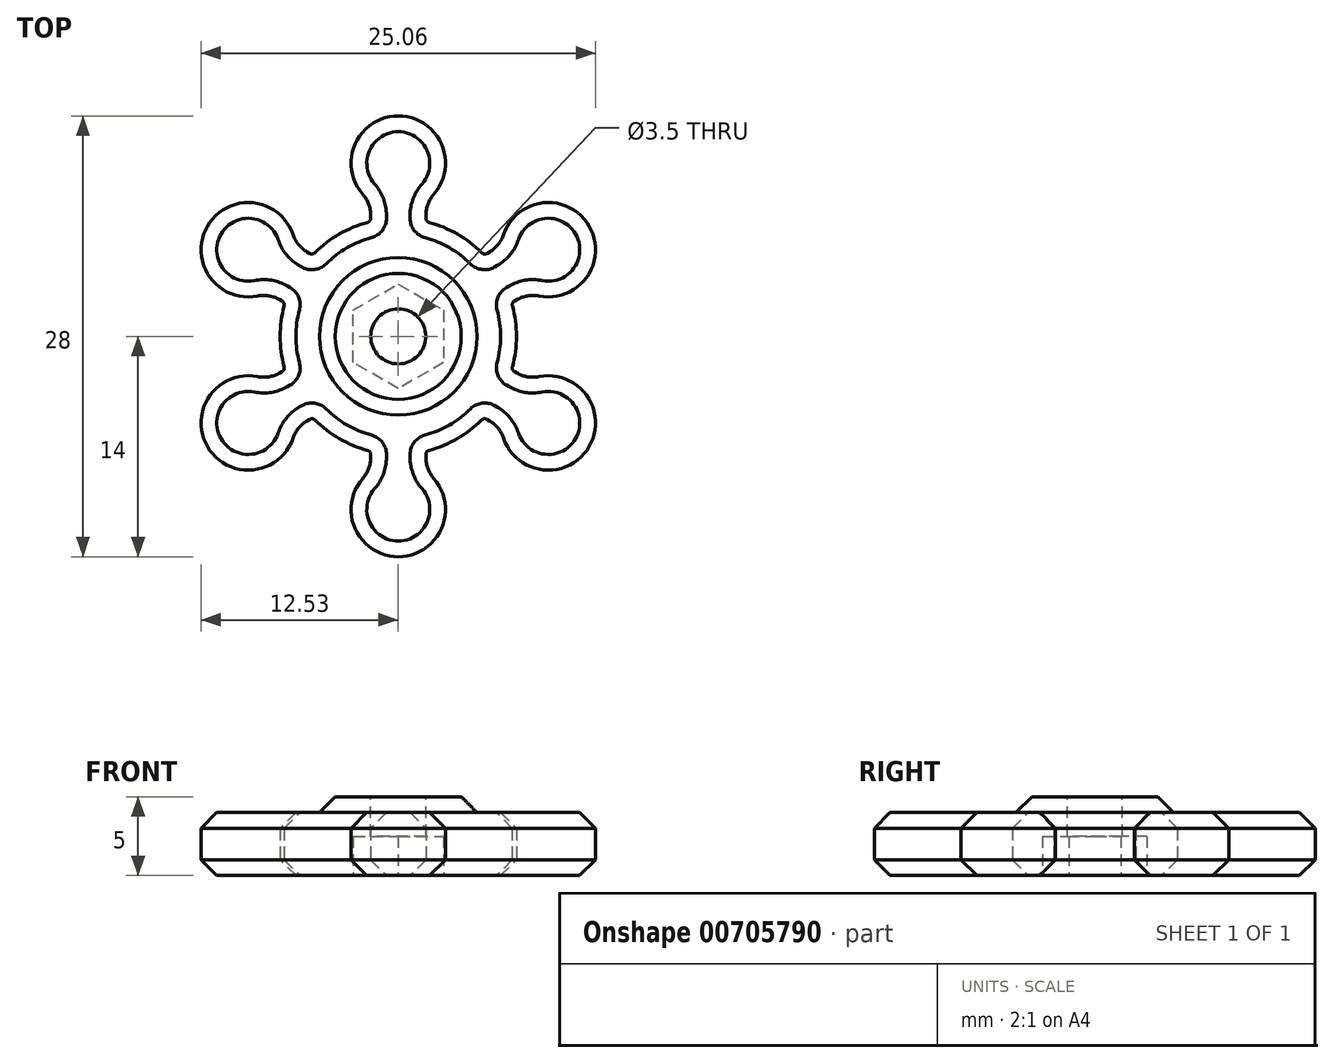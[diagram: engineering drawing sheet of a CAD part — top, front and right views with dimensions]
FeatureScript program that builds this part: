
annotation { "Feature Type Name" : "Feature", "Feature Type Description" : "" }
export const myFeature = defineFeature(function(context is Context, id is Id, definition is map)
    precondition{}
    {
        {
            var Q0;
            Q0=qCreatedBy(makeId("Top.planeOp"),FACE);
            var sketch = newSketch(context, id + "F0", { "sketchPlane" : qUnion([Q0])});
            skArc(sketch, "E0", {"start": v(-1.95, 7.24) * mm, "mid": v(-3.75, 6.5) * mm, "end": v(-5.3, 5.31) * mm});
            skArc(sketch, "E1", {"start": v(2.25, 9.02) * mm, "mid": v(0, 14) * mm, "end": v(-2.25, 9.02) * mm});
            skLineSegment(sketch, "E2.left", {"start": v(-1.75, 7.5) * mm, "end": v(-1.75, 7.7) * mm});
            skLineSegment(sketch, "E2.right", {"start": v(1.75, 7.5) * mm, "end": v(1.75, 7.7) * mm});
            skPoint(sketch, "E3.orphan", {"position": v(-1.75, 0) * mm});
            skPoint(sketch, "E4.visualSharp", {"position": v(-1.75, 8.56) * mm});
            skArc(sketch, "E4.filletArc", {"start": v(-1.75, 7.7) * mm, "mid": v(-1.88, 8.4) * mm, "end": v(-2.25, 9.02) * mm});
            skPoint(sketch, "E5.visualSharp", {"position": v(1.75, 8.56) * mm});
            skArc(sketch, "E5.filletArc", {"start": v(2.25, 9.02) * mm, "mid": v(1.88, 8.4) * mm, "end": v(1.75, 7.7) * mm});
            skPoint(sketch, "E6.visualSharp", {"position": v(1.75, 7.3) * mm});
            skArc(sketch, "E6.filletArc", {"start": v(1.75, 7.5) * mm, "mid": v(1.8, 7.34) * mm, "end": v(1.95, 7.24) * mm});
            skPoint(sketch, "E7.visualSharp", {"position": v(-1.75, 7.3) * mm});
            skArc(sketch, "E7.filletArc", {"start": v(-1.95, 7.24) * mm, "mid": v(-1.8, 7.34) * mm, "end": v(-1.75, 7.5) * mm});
            skArc(sketch, "E8.1.0", {"start": v(-6.68, 6.46) * mm, "mid": v(-12.12, 7) * mm, "end": v(-8.93, 2.56) * mm});
            skArc(sketch, "E8.1.1", {"start": v(-6.68, 6.46) * mm, "mid": v(-6.33, 5.83) * mm, "end": v(-5.79, 5.36) * mm});
            skArc(sketch, "E8.1.2", {"start": v(-7.54, 2.33) * mm, "mid": v(-8.21, 2.57) * mm, "end": v(-8.93, 2.56) * mm});
            skLineSegment(sketch, "E8.1.3", {"start": v(-7.37, 2.24) * mm, "end": v(-7.54, 2.33) * mm});
            skArc(sketch, "E8.1.4", {"start": v(-7.25, 1.93) * mm, "mid": v(-7.26, 2.1) * mm, "end": v(-7.37, 2.24) * mm});
            skLineSegment(sketch, "E8.1.5", {"start": v(-5.62, 5.27) * mm, "end": v(-5.79, 5.36) * mm});
            skArc(sketch, "E8.1.6", {"start": v(-5.62, 5.27) * mm, "mid": v(-5.45, 5.23) * mm, "end": v(-5.3, 5.31) * mm});
            skArc(sketch, "E8.2.0", {"start": v(-8.93, -2.56) * mm, "mid": v(-12.12, -7) * mm, "end": v(-6.68, -6.46) * mm});
            skArc(sketch, "E8.2.1", {"start": v(-8.93, -2.56) * mm, "mid": v(-8.21, -2.57) * mm, "end": v(-7.54, -2.33) * mm});
            skArc(sketch, "E8.2.2", {"start": v(-5.79, -5.36) * mm, "mid": v(-6.33, -5.83) * mm, "end": v(-6.68, -6.46) * mm});
            skLineSegment(sketch, "E8.2.3", {"start": v(-5.62, -5.27) * mm, "end": v(-5.79, -5.36) * mm});
            skArc(sketch, "E8.2.4", {"start": v(-5.3, -5.31) * mm, "mid": v(-5.45, -5.23) * mm, "end": v(-5.62, -5.27) * mm});
            skLineSegment(sketch, "E8.2.5", {"start": v(-7.37, -2.24) * mm, "end": v(-7.54, -2.33) * mm});
            skArc(sketch, "E8.2.6", {"start": v(-7.37, -2.24) * mm, "mid": v(-7.26, -2.1) * mm, "end": v(-7.25, -1.93) * mm});
            skArc(sketch, "E8.3.0", {"start": v(-2.25, -9.02) * mm, "mid": v(0, -14) * mm, "end": v(2.25, -9.02) * mm});
            skArc(sketch, "E8.3.1", {"start": v(-2.25, -9.02) * mm, "mid": v(-1.88, -8.4) * mm, "end": v(-1.75, -7.7) * mm});
            skArc(sketch, "E8.3.2", {"start": v(1.75, -7.7) * mm, "mid": v(1.88, -8.4) * mm, "end": v(2.25, -9.02) * mm});
            skLineSegment(sketch, "E8.3.3", {"start": v(1.75, -7.5) * mm, "end": v(1.75, -7.7) * mm});
            skArc(sketch, "E8.3.4", {"start": v(1.95, -7.24) * mm, "mid": v(1.8, -7.34) * mm, "end": v(1.75, -7.5) * mm});
            skLineSegment(sketch, "E8.3.5", {"start": v(-1.75, -7.5) * mm, "end": v(-1.75, -7.7) * mm});
            skArc(sketch, "E8.3.6", {"start": v(-1.75, -7.5) * mm, "mid": v(-1.8, -7.34) * mm, "end": v(-1.95, -7.24) * mm});
            skArc(sketch, "E8.4.0", {"start": v(6.68, -6.46) * mm, "mid": v(12.12, -7) * mm, "end": v(8.93, -2.56) * mm});
            skArc(sketch, "E8.4.1", {"start": v(6.68, -6.46) * mm, "mid": v(6.33, -5.83) * mm, "end": v(5.79, -5.36) * mm});
            skArc(sketch, "E8.4.2", {"start": v(7.54, -2.33) * mm, "mid": v(8.21, -2.57) * mm, "end": v(8.93, -2.56) * mm});
            skLineSegment(sketch, "E8.4.3", {"start": v(7.37, -2.24) * mm, "end": v(7.54, -2.33) * mm});
            skArc(sketch, "E8.4.4", {"start": v(7.25, -1.93) * mm, "mid": v(7.26, -2.1) * mm, "end": v(7.37, -2.24) * mm});
            skLineSegment(sketch, "E8.4.5", {"start": v(5.62, -5.27) * mm, "end": v(5.79, -5.36) * mm});
            skArc(sketch, "E8.4.6", {"start": v(5.62, -5.27) * mm, "mid": v(5.45, -5.23) * mm, "end": v(5.3, -5.31) * mm});
            skArc(sketch, "E8.5.0", {"start": v(8.93, 2.56) * mm, "mid": v(12.12, 7) * mm, "end": v(6.68, 6.46) * mm});
            skArc(sketch, "E8.5.1", {"start": v(8.93, 2.56) * mm, "mid": v(8.21, 2.57) * mm, "end": v(7.54, 2.33) * mm});
            skArc(sketch, "E8.5.2", {"start": v(5.79, 5.36) * mm, "mid": v(6.33, 5.83) * mm, "end": v(6.68, 6.46) * mm});
            skLineSegment(sketch, "E8.5.3", {"start": v(5.62, 5.27) * mm, "end": v(5.79, 5.36) * mm});
            skArc(sketch, "E8.5.4", {"start": v(5.3, 5.31) * mm, "mid": v(5.45, 5.23) * mm, "end": v(5.62, 5.27) * mm});
            skLineSegment(sketch, "E8.5.5", {"start": v(7.37, 2.24) * mm, "end": v(7.54, 2.33) * mm});
            skArc(sketch, "E8.5.6", {"start": v(7.37, 2.24) * mm, "mid": v(7.26, 2.1) * mm, "end": v(7.25, 1.93) * mm});
            skArc(sketch, "E9.trimOffspring", {"start": v(-7.25, 1.93) * mm, "mid": v(-7.5, 0) * mm, "end": v(-7.25, -1.93) * mm});
            skArc(sketch, "E10.trimOffspring", {"start": v(-5.3, -5.31) * mm, "mid": v(-3.75, -6.5) * mm, "end": v(-1.95, -7.24) * mm});
            skArc(sketch, "E11.trimOffspring", {"start": v(1.95, -7.24) * mm, "mid": v(3.75, -6.5) * mm, "end": v(5.3, -5.31) * mm});
            skArc(sketch, "E12.trimOffspring", {"start": v(7.25, -1.93) * mm, "mid": v(7.5, 0) * mm, "end": v(7.25, 1.93) * mm});
            skArc(sketch, "E13.trimOffspring", {"start": v(5.3, 5.31) * mm, "mid": v(3.75, 6.5) * mm, "end": v(1.95, 7.24) * mm});
            skSolve(sketch);
        }
        {
            var Q0;
            Q0=qSketchRegion(id+"F0",true);
            extrude(context, id + "F1", {"entities" : qUnion([Q0]), "depth" : 4 * mm});
        }
        {
            var Q0;
            Q0=qCreatedBy(makeId("Top.planeOp"),FACE);
            var sketch = newSketch(context, id + "F2", { "sketchPlane" : qUnion([Q0])});
            skCircle(sketch, "E14.cCircle", {"center": v(0, 0) * mm, "radius": 2.88 * mm, "construction": true});
            skLineSegment(sketch, "E14.0", {"start": v(2.88, 1.66) * mm, "end": v(2.88, -1.66) * mm});
            skLineSegment(sketch, "E14.1", {"start": v(2.88, -1.66) * mm, "end": v(0, -3.32) * mm});
            skLineSegment(sketch, "E14.2", {"start": v(0, -3.32) * mm, "end": v(-2.87, -1.66) * mm});
            skLineSegment(sketch, "E14.3", {"start": v(-2.87, -1.66) * mm, "end": v(-2.88, 1.66) * mm});
            skLineSegment(sketch, "E14.4", {"start": v(-2.88, 1.66) * mm, "end": v(0, 3.32) * mm});
            skLineSegment(sketch, "E14.5", {"start": v(0, 3.32) * mm, "end": v(2.88, 1.66) * mm});
            skPoint(sketch, "E14.0.midPoint", {"position": v(2.88, 0) * mm});
            skSolve(sketch);
        }
        {
            var Q0;
            Q0=makeQuery(id+"F2.imprint","IMPRINT",FACE,{"disambiguationData":[TD([[makeQuery(id+"F2.imprint","IMPRINT",EDGE,{"derivedFrom":sQuery(id+"F2.wireOp",EDGE,"E14.0")}),-1.0]])]});
            extrude(context, id + "F3", {"entities" : qUnion([Q0]), "operationType" : NewBodyOperationType.REMOVE, "depth" : 2.5 * mm});
        }
        {
            var Q0;
            Q0=makeQuery(id+"F1.opExtrude","CAP_FACE",FACE,{"disambiguationData":[OSD([sQuery(id+"F0.wireOp",EDGE,"E0"),sQuery(id+"F0.wireOp",EDGE,"tknGAK8U-p5LG-1uRe-C4Xr-DTzWjZsoBAFM"),sQuery(id+"F0.wireOp",EDGE,"E1"),sQuery(id+"F0.wireOp",EDGE,"E2.left"),sQuery(id+"F0.wireOp",EDGE,"E2.right"),sQuery(id+"F0.wireOp",EDGE,"E4.filletArc"),sQuery(id+"F0.wireOp",EDGE,"E5.filletArc"),sQuery(id+"F0.wireOp",EDGE,"E6.filletArc"),sQuery(id+"F0.wireOp",EDGE,"E7.filletArc"),sQuery(id+"F0.wireOp",EDGE,"E8.1.0"),sQuery(id+"F0.wireOp",EDGE,"E8.1.1"),sQuery(id+"F0.wireOp",EDGE,"E8.1.2"),sQuery(id+"F0.wireOp",EDGE,"E8.1.3"),sQuery(id+"F0.wireOp",EDGE,"E8.1.4"),sQuery(id+"F0.wireOp",EDGE,"E8.1.5"),sQuery(id+"F0.wireOp",EDGE,"E8.1.6"),sQuery(id+"F0.wireOp",EDGE,"E8.2.0"),sQuery(id+"F0.wireOp",EDGE,"E8.2.1"),sQuery(id+"F0.wireOp",EDGE,"E8.2.2"),sQuery(id+"F0.wireOp",EDGE,"E8.2.3"),sQuery(id+"F0.wireOp",EDGE,"E8.2.4"),sQuery(id+"F0.wireOp",EDGE,"E8.2.5"),sQuery(id+"F0.wireOp",EDGE,"E8.2.6"),sQuery(id+"F0.wireOp",EDGE,"E8.3.0"),sQuery(id+"F0.wireOp",EDGE,"E8.3.1"),sQuery(id+"F0.wireOp",EDGE,"E8.3.2"),sQuery(id+"F0.wireOp",EDGE,"E8.3.3"),sQuery(id+"F0.wireOp",EDGE,"E8.3.4"),sQuery(id+"F0.wireOp",EDGE,"E8.3.5"),sQuery(id+"F0.wireOp",EDGE,"E8.3.6"),sQuery(id+"F0.wireOp",EDGE,"E8.4.0"),sQuery(id+"F0.wireOp",EDGE,"E8.4.1"),sQuery(id+"F0.wireOp",EDGE,"E8.4.2"),sQuery(id+"F0.wireOp",EDGE,"E8.4.3"),sQuery(id+"F0.wireOp",EDGE,"E8.4.4"),sQuery(id+"F0.wireOp",EDGE,"E8.4.5"),sQuery(id+"F0.wireOp",EDGE,"E8.4.6"),sQuery(id+"F0.wireOp",EDGE,"E8.5.0"),sQuery(id+"F0.wireOp",EDGE,"E8.5.1"),sQuery(id+"F0.wireOp",EDGE,"E8.5.2"),sQuery(id+"F0.wireOp",EDGE,"E8.5.3"),sQuery(id+"F0.wireOp",EDGE,"E8.5.4"),sQuery(id+"F0.wireOp",EDGE,"E8.5.5"),sQuery(id+"F0.wireOp",EDGE,"E8.5.6"),sQuery(id+"F0.wireOp",EDGE,"E9.trimOffspring"),sQuery(id+"F0.wireOp",EDGE,"E10.trimOffspring"),sQuery(id+"F0.wireOp",EDGE,"E11.trimOffspring"),sQuery(id+"F0.wireOp",EDGE,"E12.trimOffspring"),sQuery(id+"F0.wireOp",EDGE,"E13.trimOffspring")])],"isStart":false});
            var sketch = newSketch(context, id + "F4", { "sketchPlane" : qUnion([Q0])});
            skCircle(sketch, "E15", {"center": v(0, 0) * mm, "radius": 4 * mm});
            skSolve(sketch);
        }
        {
            var Q0;
            Q0=qSketchRegion(id+"F4",true);
            extrude(context, id + "F5", {"entities" : qUnion([Q0]), "operationType" : NewBodyOperationType.ADD, "depth" : 1 * mm});
        }
        {
            var Q0;
            Q0=makeQuery(id+"F5.opExtrude","CAP_FACE",FACE,{"disambiguationData":[OSD([sQuery(id+"F4.wireOp",EDGE,"E15")])],"isStart":false});
            var sketch = newSketch(context, id + "F6", { "sketchPlane" : qUnion([Q0])});
            skCircle(sketch, "E16", {"center": v(0, 0) * mm, "radius": 1.75 * mm});
            skSolve(sketch);
        }
        {
            var Q0;
            Q0=qSketchRegion(id+"F6",true);
            extrude(context, id + "F7", {"entities" : qUnion([Q0]), "operationType" : NewBodyOperationType.REMOVE, "endBound" : BoundingType.THROUGH_ALL, "oppositeDirection" : true, "depth" : 25 * mm});
        }
        {
            var Q0;
            Q0=makeQuery(id+"F1.opExtrude","CAP_FACE",FACE,{"disambiguationData":[OSD([sQuery(id+"F0.wireOp",EDGE,"E0"),sQuery(id+"F0.wireOp",EDGE,"E1"),sQuery(id+"F0.wireOp",EDGE,"E2.left"),sQuery(id+"F0.wireOp",EDGE,"E2.right"),sQuery(id+"F0.wireOp",EDGE,"E4.filletArc"),sQuery(id+"F0.wireOp",EDGE,"E5.filletArc"),sQuery(id+"F0.wireOp",EDGE,"E6.filletArc"),sQuery(id+"F0.wireOp",EDGE,"E7.filletArc"),sQuery(id+"F0.wireOp",EDGE,"E8.1.0"),sQuery(id+"F0.wireOp",EDGE,"E8.1.1"),sQuery(id+"F0.wireOp",EDGE,"E8.1.2"),sQuery(id+"F0.wireOp",EDGE,"E8.1.3"),sQuery(id+"F0.wireOp",EDGE,"E8.1.4"),sQuery(id+"F0.wireOp",EDGE,"E8.1.5"),sQuery(id+"F0.wireOp",EDGE,"E8.1.6"),sQuery(id+"F0.wireOp",EDGE,"E8.2.0"),sQuery(id+"F0.wireOp",EDGE,"E8.2.1"),sQuery(id+"F0.wireOp",EDGE,"E8.2.2"),sQuery(id+"F0.wireOp",EDGE,"E8.2.3"),sQuery(id+"F0.wireOp",EDGE,"E8.2.4"),sQuery(id+"F0.wireOp",EDGE,"E8.2.5"),sQuery(id+"F0.wireOp",EDGE,"E8.2.6"),sQuery(id+"F0.wireOp",EDGE,"E8.3.0"),sQuery(id+"F0.wireOp",EDGE,"E8.3.1"),sQuery(id+"F0.wireOp",EDGE,"E8.3.2"),sQuery(id+"F0.wireOp",EDGE,"E8.3.3"),sQuery(id+"F0.wireOp",EDGE,"E8.3.4"),sQuery(id+"F0.wireOp",EDGE,"E8.3.5"),sQuery(id+"F0.wireOp",EDGE,"E8.3.6"),sQuery(id+"F0.wireOp",EDGE,"E8.4.0"),sQuery(id+"F0.wireOp",EDGE,"E8.4.1"),sQuery(id+"F0.wireOp",EDGE,"E8.4.2"),sQuery(id+"F0.wireOp",EDGE,"E8.4.3"),sQuery(id+"F0.wireOp",EDGE,"E8.4.4"),sQuery(id+"F0.wireOp",EDGE,"E8.4.5"),sQuery(id+"F0.wireOp",EDGE,"E8.4.6"),sQuery(id+"F0.wireOp",EDGE,"E8.5.0"),sQuery(id+"F0.wireOp",EDGE,"E8.5.1"),sQuery(id+"F0.wireOp",EDGE,"E8.5.2"),sQuery(id+"F0.wireOp",EDGE,"E8.5.3"),sQuery(id+"F0.wireOp",EDGE,"E8.5.4"),sQuery(id+"F0.wireOp",EDGE,"E8.5.5"),sQuery(id+"F0.wireOp",EDGE,"E8.5.6"),sQuery(id+"F0.wireOp",EDGE,"E9.trimOffspring"),sQuery(id+"F0.wireOp",EDGE,"E10.trimOffspring"),sQuery(id+"F0.wireOp",EDGE,"E11.trimOffspring"),sQuery(id+"F0.wireOp",EDGE,"E12.trimOffspring"),sQuery(id+"F0.wireOp",EDGE,"E13.trimOffspring")])],"isStart":false});
            var Q1;
            Q1=makeQuery(id+"F1.opExtrude","CAP_EDGE",EDGE,{"disambiguationData":[OSD([sQuery(id+"F0.wireOp",EDGE,"E8.2.0")])],"isStart":true});
            chamfer(context, id + "F8", {"entities" : qUnion([Q0, Q1]), "width" : 1 * mm, "tangentPropagation" : true});
        }
    });
